# Revit family: OMNIDIA
name_source: partatom
category: Communication Devices
units: mm (PartAtom-declared; Revit-internal decimal feet)

## family parameters
Cut with Voids When Loaded = No
Host = Face
Maintain Annotation Orientation = No
OmniClass Number = 23.85.80.11.27
OmniClass Title = Lighting Controls
Part Type = Normal
Room Calculation Point = No
Round Connector Dimension = Use Diameter
Shared = Yes

## types (1)
- OMNIDIA
    Assembly Code = D5090
    Certifications = UL and cUL listed
    Coverage = 450 sq ft
    Default Elevation = 48 "
    Description = The OMNIDIA combines passive infrared (PIR) and acoustic (sound-activated) technologies to turn lighting systems on and off based on occupancy. The OMNIDIA features Control Solutions' patented IntelliDAPT technology, which makes all the sensor adjustments automatically. Throughout the product's lifespan, smart software analyzes the controlled area and makes digital adjustments to sensitivity and timer settings. Occupancy sensors with IntelliDAPT provide a maintenance-free Install and Forget operation.
    Features = • IntelliDAPT® self-adaptive technology—no manual adjustment required
• All-digital dual technology acoustic and passive infrared (PIR) sensor
• Non-volatile memory for sensor settings
• Low Voltage device: 24VDC
• 450 square-foot coverage
• Optional relay and photocell control
• UL and cUL listed
• 5 year warranty
    Housing Material = Paint -  Matte White
    Manufacturer = NX Lighting Controls
    Model = OMNNIDIA
    Mounting Height = 8 - 12 ft
    Sensing Element = Paint -  Matte White
    Type Comments = CEILING MOUNT OCCUPANCY SENSORS
    URL = https://www.currentlighting.com
    Voltage Rating = 24V
    Warranty = 5-Years Warranty
    Width = 4.5 "

## geometry (parser evidence)
native form markers: Sweep x3
no freeform markers — native parametric forms only
